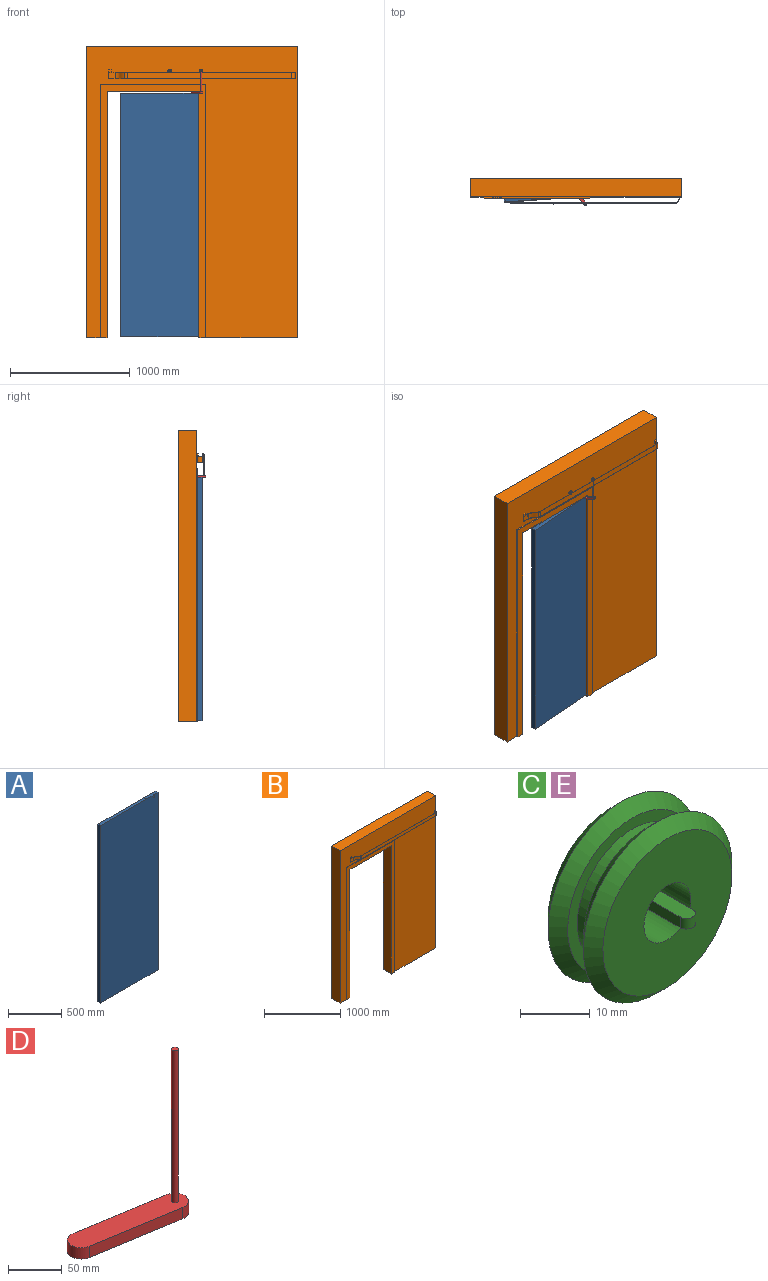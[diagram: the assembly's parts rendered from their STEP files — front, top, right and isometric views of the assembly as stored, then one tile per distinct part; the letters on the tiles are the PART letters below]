
ASSEMBLY  parts=5 mates=5
PART A: 10 faces, bbox 762x34.9x2032 mm
  f0: plane 762x34.93mm, normal (0,0,1), area 26470.3mm2, adj f1,f3,f4,f5,f7,f8
  f1: plane 2032x34.93mm, normal (-1,0,0), area 70967.6mm2, adj f0,f2,f4,f5
  f2: plane 762x34.93mm, normal (0,0,-1), area 26612.8mm2, adj f1,f3,f4,f5
  f3: plane 2032x34.93mm, normal (1,0,0), area 70967.6mm2, adj f0,f2,f4,f5
  f4: plane 2032x762mm, normal (0,-1,0), area 1548222.7mm2, adj f0,f1,f2,f3,f6,f7
  f5: plane 2032x762mm, normal (0,1,0), area 1548384mm2, adj f0,f1,f2,f3
  f6: plane 6.35x3.18mm, normal (0,0,1), area 15.8mm2, adj f4,f7
  f7: cylinder r=3.17mm len=25.4mm, axis (0,0,1), area 253.4mm2, adj f0,f4,f6
  f8: cylinder r=6.35mm len=25.4mm, axis (0,0,1), area 1013.4mm2, adj f0,f9
  f9: plane 12.7x12.7mm, normal (0,0,1), area 126.7mm2, adj f8
PART B: 56 faces, bbox 1762.1x206.4x2438.4 mm
  f0: plane 1525.11x53.98mm, normal (0,0,1), area 5009.5mm2, adj f1,f2,f19,f21,f22,f23,f25,f26
  f1: plane 55.88x50.8mm, normal (0,1,0), area 2834.5mm2, adj f0,f23,f24,f33,f34,f37,f54,f55
  f2: plane 55.88x50.8mm, normal (0,-1,0), area 2834.5mm2, adj f0,f24,f25,f33,f37,f39,f54,f55
  f3: plane 2114.55x11.11mm, normal (-1,0,0), area 23497.9mm2, adj f4,f10,f11,f19
  f4: plane 172.24x163.51mm, normal (0,0,-1), area 26249.9mm2, adj f3,f5,f11,f15,f16,f18,f19,f20
  f5: plane 2057.4x152.4mm, normal (1,0,0), area 313547.8mm2, adj f4,f6,f11,f20
  f6: plane 765.97x152.4mm, normal (0,0,-1), area 116733.6mm2, adj f5,f7,f11,f20
  f7: plane 2057.4x152.4mm, normal (-1,0,0), area 313547.8mm2, adj f6,f8,f11,f20
  f8: plane 823.91x163.51mm, normal (0,0,-1), area 125564.3mm2, adj f7,f9,f11,f12,f13,f18,f19,f20
  f9: plane 2114.55x11.11mm, normal (1,0,0), area 23497.9mm2, adj f8,f10,f11,f19
  f10: plane 880.27x11.11mm, normal (0,0,1), area 9782mm2, adj f3,f9,f11,f19
  f11: plane 2114.55x880.27mm, normal (0,-1,0), area 285468.2mm2, adj f3,f4,f5,f6,f7,f8,f9,f10
  f12: plane 2114.55x11.11mm, normal (-1,0,0), area 23497.9mm2, adj f8,f17,f18,f20
  f13: plane 2438.4x152.4mm, normal (1,0,0), area 371612.2mm2, adj f8,f14,f18,f19
  f14: plane 1762.13x152.4mm, normal (0,0,1), area 268547.8mm2, adj f13,f15,f18,f19
  f15: plane 2438.4x152.4mm, normal (-1,0,0), area 371612.2mm2, adj f4,f14,f18,f19
  f16: plane 2114.55x11.11mm, normal (1,0,0), area 23497.9mm2, adj f4,f17,f18,f20
  f17: plane 880.27x11.11mm, normal (0,0,-1), area 9782mm2, adj f12,f16,f18,f20
  f18: plane 2438.4x1762.13mm, normal (0,1,0), area 2435393.3mm2, adj f4,f8,f12,f13,f14,f15,f16,f17
  f19: plane 2438.4x1762.13mm, normal (0,-1,0), area 2435036.2mm2, adj f0,f3,f4,f8,f9,f10,f13,f14
  f20: plane 2114.55x880.27mm, normal (0,1,0), area 285468.2mm2, adj f4,f5,f6,f7,f8,f12,f16,f17
  f21: cylinder r=25.4mm len=50.8mm, axis (0,0,-1), area 1517.4mm2, adj f0,f22,f32,f33
  f22: plane 1371.44x50.8mm, normal (0,1,0), area 69669.2mm2, adj f0,f21,f23,f33
  f23: extruded ~101.6x50.8mm, area 5792.4mm2, adj f0,f1,f22,f33
  f24: plane 74.93x3.92mm, normal (-1,0,0), area 255.9mm2, adj f1,f2,f33,f34,f39,f44,f49,f53
  f25: extruded ~79.81x50.8mm, area 4669.5mm2, adj f0,f2,f26,f33
  f26: extruded ~50.8x21.79mm, area 1123mm2, adj f0,f25,f27,f33
  f27: plane 1371.44x50.8mm, normal (0,-1,0), area 69669.2mm2, adj f0,f26,f28,f33
  f28: cylinder r=28.57mm len=50.8mm, axis (0,0,-1), area 1707.1mm2, adj f0,f27,f29,f33
  f29: plane 50.8x16.41mm, normal (0.92,-0.38,0), area 902.8mm2, adj f0,f28,f30,f33
  f30: plane 50.8x19.99mm, normal (0.97,-0.24,0), area 1045.2mm2, adj f0,f19,f29,f33
  f31: plane 50.8x16.87mm, normal (-1,0,0), area 857.2mm2, adj f0,f19,f32,f33
  f32: plane 50.8x18.3mm, normal (-0.92,0.38,0), area 1006.9mm2, adj f0,f21,f31,f33
  f33: plane 1567.02x53.98mm, normal (0,0,-1), area 5142.6mm2, adj f1,f2,f19,f21,f22,f23,f24,f25
  f34: plane 25.4x0.2mm, normal (0,0,-1), area 5mm2, adj f1,f24,f37,f52
  f35: plane 22.86x22.86mm, normal (0,1,0), area 522.6mm2, adj f48,f50,f52,f53
  f36: plane 22.86x22.86mm, normal (0,-1,0), area 522.6mm2, adj f40,f41,f43,f44
  f37: plane 24.38x3.92mm, normal (1,0,0), area 95.4mm2, adj f1,f2,f34,f39,f40,f45,f50,f55
  f38: plane 22.86x3.92mm, normal (0,0,1), area 89.6mm2, adj f43,f45,f48,f49
  f39: plane 25.4x0.55mm, normal (0,0,-1), area 14mm2, adj f2,f24,f37,f41
  f40: cylinder r=1.27mm len=24.13mm, axis (0,0,1), area 47.2mm2, adj f36,f37,f41,f42
  f41: cylinder r=1.27mm len=25.4mm, axis (1,0,0), area 48.8mm2, adj f36,f39,f40,f44
  f42: sphere r=1.27mm, area 2.5mm2, adj f40,f43,f45
  f43: cylinder r=1.27mm len=22.86mm, axis (-1,0,0), area 45.6mm2, adj f36,f38,f42,f46
  f44: cylinder r=1.27mm len=24.13mm, axis (0,0,1), area 47.2mm2, adj f24,f36,f41,f46
  f45: cylinder r=1.27mm len=3.92mm, axis (0,-1,0), area 7.8mm2, adj f37,f38,f42,f47
  f46: sphere r=1.27mm, area 2.5mm2, adj f43,f44,f49
  f47: sphere r=1.27mm, area 2.5mm2, adj f45,f48,f50
  f48: cylinder r=1.27mm len=22.86mm, axis (1,0,0), area 45.6mm2, adj f35,f38,f47,f51
  f49: cylinder r=1.27mm len=3.92mm, axis (0,-1,0), area 7.8mm2, adj f24,f38,f46,f51
  f50: cylinder r=1.27mm len=24.13mm, axis (0,0,-1), area 47.2mm2, adj f35,f37,f47,f52
  f51: sphere r=1.27mm, area 2.5mm2, adj f48,f49,f53
  f52: cylinder r=1.27mm len=25.4mm, axis (-1,0,0), area 48.8mm2, adj f34,f35,f50,f53
  f53: cylinder r=1.27mm len=24.13mm, axis (0,0,-1), area 47.2mm2, adj f24,f35,f51,f52
  f54: plane 3.18x0.25mm, normal (-1,0,0), area 0.8mm2, adj f0,f1,f2,f55
  f55: plane 16.51x3.18mm, normal (0,0,1), area 52.4mm2, adj f1,f2,f37,f54
PART C: 18 faces, bbox 30.1x16.3x30.1 mm
  f0: cylinder r=0.89mm len=4.76mm, axis (0,0,-1), area 21.3mm2, adj f1,f11,f12,f13,f16
  f1: cylinder r=4.76mm len=11.11mm, axis (0,-1,0), area 330mm2, adj f0,f2,f10
  f2: plane 26.18x26.18mm, normal (0,-1,0), area 467.1mm2, adj f1,f3
  f3: cone r=15.07mm half-angle=45deg, axis (0,1,0), area 248.3mm2, adj f2,f4
  f4: cone r=13.09mm half-angle=45deg, axis (0,-1,0), area 248.3mm2, adj f3,f5
  f5: plane 26.18x26.18mm, normal (0,1,0), area 148.7mm2, adj f4,f6
  f6: cylinder r=11.14mm len=22.27mm, axis (0,-1,0), area 222.2mm2, adj f5,f7
  f7: plane 26.18x26.18mm, normal (0,-1,0), area 148.7mm2, adj f6,f8
  f8: cone r=15.07mm half-angle=45deg, axis (0,1,0), area 248.3mm2, adj f7,f9
  f9: cone r=13.09mm half-angle=45deg, axis (0,-1,0), area 248.3mm2, adj f8,f10
  f10: plane 26.18x26.18mm, normal (0,1,0), area 467.1mm2, adj f1,f9
  f11: plane 11.62x2.6mm, normal (0,0,-1), area 28.4mm2, adj f0,f12,f13,f14,f15,f17
  f12: plane 1.85x0.41mm, normal (0,1,0), area 0.8mm2, adj f0,f11,f14,f16
  f13: plane 1.85x0.41mm, normal (0,1,0), area 0.8mm2, adj f0,f11,f15,f16
  f14: plane 9.42x1.85mm, normal (-1,0,0), area 17.4mm2, adj f11,f12,f16,f17
  f15: plane 9.42x1.85mm, normal (1,0,0), area 17.4mm2, adj f11,f13,f16,f17
  f16: plane 10.72x2.6mm, normal (0,0,1), area 25.9mm2, adj f0,f12,f13,f14,f15,f17
  f17: cylinder r=1.3mm len=2.6mm, axis (0,0,1), area 7.6mm2, adj f11,f14,f15,f16
PART D: 8 faces, bbox 130.9x42.9x185.4 mm
  f0: plane 6.35x6.35mm, normal (0,0,1), area 31.7mm2, adj f1
  f1: cylinder r=3.17mm len=172.72mm, axis (0,0,-1), area 3445.6mm2, adj f0,f6
  f2: cylinder r=12.7mm len=25.23mm, axis (0,0,-1), area 506.7mm2, adj f3,f5,f6,f7
  f3: plane 105.54x17.46mm, normal (-0.16,-0.99,0), area 1358.5mm2, adj f2,f4,f6,f7
  f4: cylinder r=12.7mm len=25.23mm, axis (0,0,-1), area 506.7mm2, adj f3,f5,f6,f7
  f5: plane 105.54x17.46mm, normal (0.16,0.99,0), area 1358.5mm2, adj f2,f4,f6,f7
  f6: plane 130.94x42.86mm, normal (0,0,1), area 3192.1mm2, adj f1,f2,f3,f4,f5
  f7: plane 130.94x42.86mm, normal (0,0,-1), area 3223.8mm2, adj f2,f3,f4,f5
PART E: same geometry as C
PLACE A rot(axis=(0,0,1),4.4deg) t=(-219.05,18.98,-191.38)mm
PLACE B at identity fixed
PLACE C t=(76.78,-52.39,1010.04)mm
PLACE D rot(axis=(0,0,-1),39.4deg) t=(-156.27,174.71,-191.38)mm
PLACE E rot(axis=(0,0,1),0deg) t=(-185.67,-52.39,1010.04)mm
MATE planar D.f1 <-> C.f17  axis (0,0,1) through (76.78,-61.81,1010.04)mm
MATE parallel B.f0 <-> E.f0  axis (0,0,1) through (119.55,-49.2,996.95)mm
MATE cylindrical D.f1 <-> C.f17  axis (0,0,1) through (76.78,-61.81,1010.04)mm
MATE cylindrical D.f2 <-> A.f8  axis (0,0,-1) through (6.3,18.65,824.62)mm
MATE parallel B.f0 <-> C.f0  axis (0,0,1) through (119.55,-49.2,996.95)mm
